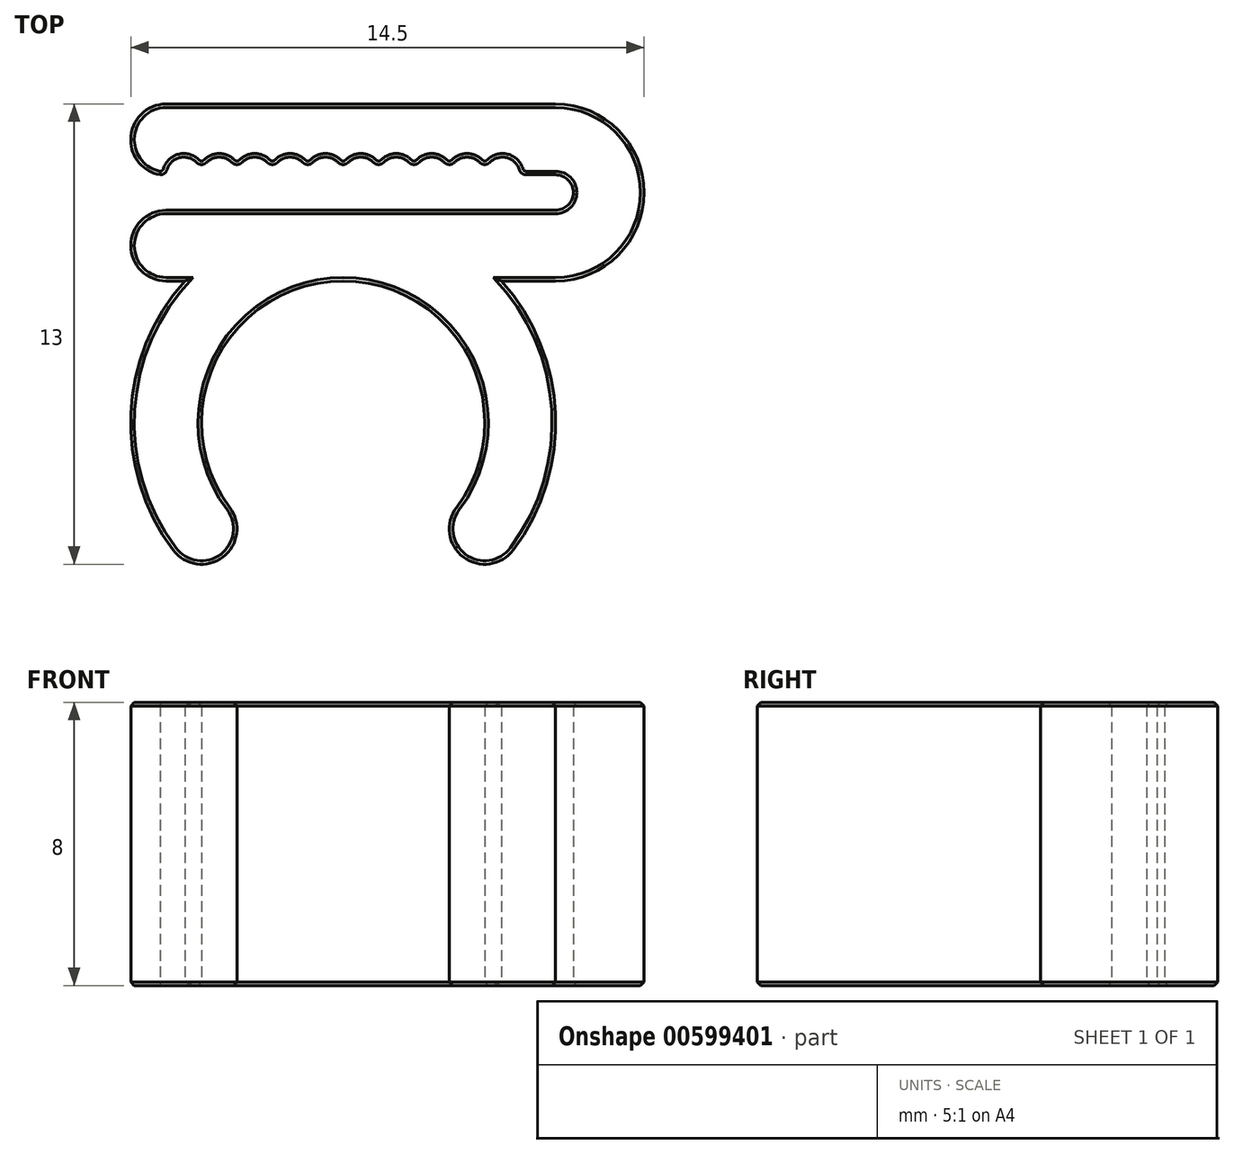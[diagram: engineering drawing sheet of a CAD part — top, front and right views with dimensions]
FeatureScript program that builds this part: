
annotation { "Feature Type Name" : "Feature", "Feature Type Description" : "" }
export const myFeature = defineFeature(function(context is Context, id is Id, definition is map)
    precondition{}
    {
        {
            var Q0;
            Q0=qCreatedBy(makeId("Top.planeOp"),FACE);
            var sketch = newSketch(context, id + "F0", { "sketchPlane" : qUnion([Q0])});
            skCircle(sketch, "E0", {"center": v(0, 0) * mm, "radius": 4 * mm});
            skCircle(sketch, "E1", {"center": v(0, 0) * mm, "radius": 6 * mm});
            skLineSegment(sketch, "E2.bottom", {"start": v(3, -2.65) * mm, "end": v(-3, -2.65) * mm});
            skLineSegment(sketch, "E2.top", {"start": v(3, -6) * mm, "end": v(-3, -6) * mm});
            skLineSegment(sketch, "E2.left", {"start": v(3, -2.65) * mm, "end": v(3, -6) * mm});
            skLineSegment(sketch, "E2.right", {"start": v(-3, -2.65) * mm, "end": v(-3, -6) * mm});
            skPoint(sketch, "E2.middle", {"position": v(0, -4.32) * mm});
            skLineSegment(sketch, "E3.bottom", {"start": v(6, 6) * mm, "end": v(-6, 6) * mm});
            skLineSegment(sketch, "E3.top", {"start": v(6, 4) * mm, "end": v(-6, 4) * mm});
            skLineSegment(sketch, "E3.left", {"start": v(6, 6) * mm, "end": v(6, 4) * mm});
            skLineSegment(sketch, "E3.right", {"start": v(-6, 6) * mm, "end": v(-6, 4) * mm});
            skPoint(sketch, "E3.middle", {"position": v(0, 5) * mm});
            skLineSegment(sketch, "E4.bottom", {"start": v(6, 7) * mm, "end": v(-6, 7) * mm});
            skLineSegment(sketch, "E4.top", {"start": v(6, 9) * mm, "end": v(-6, 9) * mm});
            skLineSegment(sketch, "E4.left", {"start": v(6, 7) * mm, "end": v(6, 9) * mm});
            skLineSegment(sketch, "E4.right", {"start": v(-6, 7) * mm, "end": v(-6, 9) * mm});
            skPoint(sketch, "E4.middle", {"position": v(0, 8) * mm});
            skCircle(sketch, "E5", {"center": v(6, 6.5) * mm, "radius": 2.5 * mm});
            skCircle(sketch, "E6", {"center": v(-4.5, 7) * mm, "radius": 0.5 * mm});
            skCircle(sketch, "E7.1.0.0", {"center": v(-3.5, 7) * mm, "radius": 0.5 * mm});
            skCircle(sketch, "E7.2.0.0", {"center": v(-2.5, 7) * mm, "radius": 0.5 * mm});
            skCircle(sketch, "E7.3.0.0", {"center": v(-1.5, 7) * mm, "radius": 0.5 * mm});
            skCircle(sketch, "E7.4.0.0", {"center": v(-0.5, 7) * mm, "radius": 0.5 * mm});
            skLineSegment(sketch, "E7.direction1", {"start": v(-4.5, 7) * mm, "end": v(-3.5, 7) * mm, "construction": true});
            skCircle(sketch, "E8.0.5.0", {"center": v(0.5, 7) * mm, "radius": 0.5 * mm});
            skCircle(sketch, "E8.0.6.0", {"center": v(1.5, 7) * mm, "radius": 0.5 * mm});
            skCircle(sketch, "E8.0.7.0", {"center": v(2.5, 7) * mm, "radius": 0.5 * mm});
            skCircle(sketch, "E9", {"center": v(6, 6.5) * mm, "radius": 0.5 * mm});
            skCircle(sketch, "E10.0.8.0", {"center": v(3.5, 7) * mm, "radius": 0.5 * mm});
            skCircle(sketch, "E10.0.9.0", {"center": v(4.5, 7) * mm, "radius": 0.5 * mm});
            skSolve(sketch);
        }
        {
            var Q0;
            {var subQ16=sQuery(id+"F0.wireOp",EDGE,"E4.top");Q0=makeQuery(id+"F0.imprint","IMPRINT",FACE,{"disambiguationData":[TD([[makeQuery(id+"F0.imprint","IMPRINT",EDGE,{"derivedFrom":subQ16}),1.0]])]});}
            var Q1;
            {var subQ1=sQuery(id+"F0.wireOp",EDGE,"E4.left");Q1=makeQuery(id+"F0.imprint","IMPRINT",FACE,{"disambiguationData":[TD([[makeQuery(id+"F0.imprint","IMPRINT",EDGE,{"derivedFrom":subQ1}),1.0]])]});}
            var Q2;
            {var subQ0=sQuery(id+"F0.wireOp",EDGE,"E3.left");Q2=makeQuery(id+"F0.imprint","IMPRINT",FACE,{"disambiguationData":[TD([[makeQuery(id+"F0.imprint","IMPRINT",EDGE,{"derivedFrom":subQ0}),1.0]])]});}
            var Q3;
            {var subQ0=sQuery(id+"F0.wireOp",EDGE,"E3.left");Q3=makeQuery(id+"F0.imprint","IMPRINT",FACE,{"disambiguationData":[TD([[makeQuery(id+"F0.imprint","IMPRINT",EDGE,{"derivedFrom":subQ0}),-1.0]])]});}
            var Q4;
            {var subQ0=sQuery(id+"F0.wireOp",EDGE,"E3.bottom");var subQ1=sQuery(id+"F0.wireOp",EDGE,"E1");var subQ2=makeQuery(id+"F0.imprint","INTERSECT",VERTEX,{"derivedFrom":[subQ1,subQ0]});Q4=makeQuery(id+"F0.imprint","IMPRINT",FACE,{"disambiguationData":[TD([[makeQuery(id+"F0.imprint","IMPRINT",EDGE,{"disambiguationData":[TD([[subQ2,1.0]])],"derivedFrom":subQ1}),-1.0]])]});}
            var Q5;
            {var subQ0=sQuery(id+"F0.wireOp",EDGE,"E1");var subQ1=makeQuery(id+"F0.imprint","INTERSECT",VERTEX,{"derivedFrom":[subQ0,sQuery(id+"F0.wireOp",EDGE,"E3.bottom")]});Q5=makeQuery(id+"F0.imprint","IMPRINT",FACE,{"disambiguationData":[TD([[makeQuery(id+"F0.imprint","IMPRINT",EDGE,{"disambiguationData":[TD([[subQ1,1.0]])],"derivedFrom":subQ0}),1.0]])]});}
            var Q6;
            {var subQ5=sQuery(id+"F0.wireOp",EDGE,"E3.right");Q6=makeQuery(id+"F0.imprint","IMPRINT",FACE,{"disambiguationData":[TD([[makeQuery(id+"F0.imprint","IMPRINT",EDGE,{"derivedFrom":subQ5}),1.0]])]});}
            var Q7;
            {var subQ3=sQuery(id+"F0.wireOp",EDGE,"E3.top");var subQ5=sQuery(id+"F0.wireOp",EDGE,"E1");var subQ6=makeQuery(id+"F0.imprint","INTERSECT",VERTEX,{"disambiguationData":[OD(1.0)],"derivedFrom":[subQ5,subQ3]});Q7=makeQuery(id+"F0.imprint","IMPRINT",FACE,{"disambiguationData":[TD([[makeQuery(id+"F0.imprint","IMPRINT",EDGE,{"disambiguationData":[TD([[subQ6,-1.0]])],"derivedFrom":subQ5}),1.0]])]});}
            var Q8;
            {var subQ3=sQuery(id+"F0.wireOp",EDGE,"E3.top");var subQ5=sQuery(id+"F0.wireOp",EDGE,"E1");var subQ7=makeQuery(id+"F0.imprint","INTERSECT",VERTEX,{"disambiguationData":[OD(0.0)],"derivedFrom":[subQ5,subQ3]});Q8=makeQuery(id+"F0.imprint","IMPRINT",FACE,{"disambiguationData":[TD([[makeQuery(id+"F0.imprint","IMPRINT",EDGE,{"disambiguationData":[TD([[subQ7,1.0]])],"derivedFrom":subQ5}),1.0]])]});}
            extrude(context, id + "F1", {"entities" : qUnion([Q0, Q1, Q2, Q3, Q4, Q5, Q6, Q7, Q8]), "depth" : 8 * mm, "offsetDistance" : 25 * mm});
        }
        {
            var Q0;
            Q0=makeQuery(id+"F1.opExtrude","SWEPT_EDGE",EDGE,{"disambiguationData":[OSD([sQuery(id+"F0.wireOp",EDGE,"E4.bottom"),sQuery(id+"F0.wireOp",EDGE,"E6"),sQuery(id+"F0.wireOp",EDGE,"E7.1.0.0")])]});
            var Q1;
            Q1=makeQuery(id+"F1.opExtrude","SWEPT_EDGE",EDGE,{"disambiguationData":[OSD([sQuery(id+"F0.wireOp",EDGE,"E4.bottom"),sQuery(id+"F0.wireOp",EDGE,"E7.1.0.0"),sQuery(id+"F0.wireOp",EDGE,"E7.2.0.0")])]});
            var Q2;
            Q2=makeQuery(id+"F1.opExtrude","SWEPT_EDGE",EDGE,{"disambiguationData":[OSD([sQuery(id+"F0.wireOp",EDGE,"E4.bottom"),sQuery(id+"F0.wireOp",EDGE,"E7.2.0.0"),sQuery(id+"F0.wireOp",EDGE,"E7.3.0.0")])]});
            var Q3;
            Q3=makeQuery(id+"F1.opExtrude","SWEPT_EDGE",EDGE,{"disambiguationData":[OSD([sQuery(id+"F0.wireOp",EDGE,"E4.bottom"),sQuery(id+"F0.wireOp",EDGE,"E7.3.0.0"),sQuery(id+"F0.wireOp",EDGE,"E7.4.0.0")])]});
            var Q4;
            Q4=makeQuery(id+"F1.opExtrude","SWEPT_EDGE",EDGE,{"disambiguationData":[OSD([sQuery(id+"F0.wireOp",EDGE,"E4.bottom"),sQuery(id+"F0.wireOp",EDGE,"E7.4.0.0"),sQuery(id+"F0.wireOp",EDGE,"E8.0.5.0")])]});
            var Q5;
            Q5=makeQuery(id+"F1.opExtrude","SWEPT_EDGE",EDGE,{"disambiguationData":[OSD([sQuery(id+"F0.wireOp",EDGE,"E4.bottom"),sQuery(id+"F0.wireOp",EDGE,"E8.0.5.0"),sQuery(id+"F0.wireOp",EDGE,"E8.0.6.0")])]});
            var Q6;
            Q6=makeQuery(id+"F1.opExtrude","SWEPT_EDGE",EDGE,{"disambiguationData":[OSD([sQuery(id+"F0.wireOp",EDGE,"E4.bottom"),sQuery(id+"F0.wireOp",EDGE,"E8.0.6.0"),sQuery(id+"F0.wireOp",EDGE,"E8.0.7.0")])]});
            var Q7;
            Q7=makeQuery(id+"F1.opExtrude","SWEPT_EDGE",EDGE,{"disambiguationData":[OSD([sQuery(id+"F0.wireOp",EDGE,"E4.bottom"),sQuery(id+"F0.wireOp",EDGE,"E8.0.7.0"),sQuery(id+"F0.wireOp",EDGE,"E10.0.8.0")])]});
            var Q8;
            Q8=makeQuery(id+"F1.opExtrude","SWEPT_EDGE",EDGE,{"disambiguationData":[OSD([sQuery(id+"F0.wireOp",EDGE,"E4.bottom"),sQuery(id+"F0.wireOp",EDGE,"E10.0.8.0"),sQuery(id+"F0.wireOp",EDGE,"E10.0.9.0")])]});
            var Q9;
            Q9=makeQuery(id+"F1.opExtrude","SWEPT_EDGE",EDGE,{"disambiguationData":[OSD([sQuery(id+"F0.wireOp",EDGE,"E4.bottom"),sQuery(id+"F0.wireOp",EDGE,"E6")])]});
            var Q10;
            Q10=makeQuery(id+"F1.opExtrude","SWEPT_EDGE",EDGE,{"disambiguationData":[OSD([sQuery(id+"F0.wireOp",EDGE,"E4.bottom"),sQuery(id+"F0.wireOp",EDGE,"E10.0.9.0")])]});
            fillet(context, id + "F2", {"entities" : qUnion([Q0, Q1, Q2, Q3, Q4, Q5, Q6, Q7, Q8, Q9, Q10]), "radius" : 0.2 * mm, "tangentPropagation" : true, "allowEdgeOverflow" : false});
        }
        {
            var Q0;
            Q0=makeQuery(id+"F1.opExtrude","SWEPT_EDGE",EDGE,{"disambiguationData":[OSD([sQuery(id+"F0.wireOp",EDGE,"E4.bottom"),sQuery(id+"F0.wireOp",EDGE,"E4.right")])]});
            var Q1;
            Q1=makeQuery(id+"F1.opExtrude","SWEPT_EDGE",EDGE,{"disambiguationData":[OSD([sQuery(id+"F0.wireOp",EDGE,"E4.top"),sQuery(id+"F0.wireOp",EDGE,"E4.right")])]});
            var Q2;
            Q2=makeQuery(id+"F1.opExtrude","SWEPT_EDGE",EDGE,{"disambiguationData":[OSD([sQuery(id+"F0.wireOp",EDGE,"E3.bottom"),sQuery(id+"F0.wireOp",EDGE,"E3.right")])]});
            var Q3;
            Q3=makeQuery(id+"F1.opExtrude","SWEPT_EDGE",EDGE,{"disambiguationData":[OSD([sQuery(id+"F0.wireOp",EDGE,"E3.top"),sQuery(id+"F0.wireOp",EDGE,"E3.right")])]});
            var Q4;
            Q4=makeQuery(id+"F1.opExtrude","SWEPT_EDGE",EDGE,{"disambiguationData":[OSD([sQuery(id+"F0.wireOp",EDGE,"E0"),sQuery(id+"F0.wireOp",EDGE,"E2.bottom"),sQuery(id+"F0.wireOp",EDGE,"E2.right")])]});
            var Q5;
            Q5=makeQuery(id+"F1.opExtrude","SWEPT_EDGE",EDGE,{"disambiguationData":[OSD([sQuery(id+"F0.wireOp",EDGE,"E1"),sQuery(id+"F0.wireOp",EDGE,"E2.right")])]});
            var Q6;
            Q6=makeQuery(id+"F1.opExtrude","SWEPT_EDGE",EDGE,{"disambiguationData":[OSD([sQuery(id+"F0.wireOp",EDGE,"E1"),sQuery(id+"F0.wireOp",EDGE,"E2.left")])]});
            var Q7;
            Q7=makeQuery(id+"F1.opExtrude","SWEPT_EDGE",EDGE,{"disambiguationData":[OSD([sQuery(id+"F0.wireOp",EDGE,"E0"),sQuery(id+"F0.wireOp",EDGE,"E2.bottom"),sQuery(id+"F0.wireOp",EDGE,"E2.left")])]});
            fillet(context, id + "F3", {"entities" : qUnion([Q0, Q1, Q2, Q3, Q4, Q5, Q6, Q7]), "radius" : 1 * mm, "tangentPropagation" : true, "allowEdgeOverflow" : false});
        }
        {
            var Q0;
            Q0=makeQuery(id+"F1.opExtrude","CAP_FACE",FACE,{"disambiguationData":[OSD([sQuery(id+"F0.wireOp",EDGE,"E0"),sQuery(id+"F0.wireOp",EDGE,"E1"),sQuery(id+"F0.wireOp",EDGE,"E2.left"),sQuery(id+"F0.wireOp",EDGE,"E2.right"),sQuery(id+"F0.wireOp",EDGE,"E3.bottom"),sQuery(id+"F0.wireOp",EDGE,"E3.top"),sQuery(id+"F0.wireOp",EDGE,"E3.right"),sQuery(id+"F0.wireOp",EDGE,"E4.bottom"),sQuery(id+"F0.wireOp",EDGE,"E4.top"),sQuery(id+"F0.wireOp",EDGE,"E4.right"),sQuery(id+"F0.wireOp",EDGE,"E5"),sQuery(id+"F0.wireOp",EDGE,"E6"),sQuery(id+"F0.wireOp",EDGE,"E7.1.0.0"),sQuery(id+"F0.wireOp",EDGE,"E7.2.0.0"),sQuery(id+"F0.wireOp",EDGE,"E7.3.0.0"),sQuery(id+"F0.wireOp",EDGE,"E7.4.0.0"),sQuery(id+"F0.wireOp",EDGE,"E8.0.5.0"),sQuery(id+"F0.wireOp",EDGE,"E8.0.6.0"),sQuery(id+"F0.wireOp",EDGE,"E8.0.7.0"),sQuery(id+"F0.wireOp",EDGE,"E9"),sQuery(id+"F0.wireOp",EDGE,"E10.0.8.0"),sQuery(id+"F0.wireOp",EDGE,"E10.0.9.0")])],"isStart":false});
            var Q1;
            Q1=makeQuery(id+"F1.opExtrude","CAP_FACE",FACE,{"disambiguationData":[OSD([sQuery(id+"F0.wireOp",EDGE,"E0"),sQuery(id+"F0.wireOp",EDGE,"E1"),sQuery(id+"F0.wireOp",EDGE,"E2.left"),sQuery(id+"F0.wireOp",EDGE,"E2.right"),sQuery(id+"F0.wireOp",EDGE,"E3.bottom"),sQuery(id+"F0.wireOp",EDGE,"E3.top"),sQuery(id+"F0.wireOp",EDGE,"E3.right"),sQuery(id+"F0.wireOp",EDGE,"E4.bottom"),sQuery(id+"F0.wireOp",EDGE,"E4.top"),sQuery(id+"F0.wireOp",EDGE,"E4.right"),sQuery(id+"F0.wireOp",EDGE,"E5"),sQuery(id+"F0.wireOp",EDGE,"E6"),sQuery(id+"F0.wireOp",EDGE,"E7.1.0.0"),sQuery(id+"F0.wireOp",EDGE,"E7.2.0.0"),sQuery(id+"F0.wireOp",EDGE,"E7.3.0.0"),sQuery(id+"F0.wireOp",EDGE,"E7.4.0.0"),sQuery(id+"F0.wireOp",EDGE,"E8.0.5.0"),sQuery(id+"F0.wireOp",EDGE,"E8.0.6.0"),sQuery(id+"F0.wireOp",EDGE,"E8.0.7.0"),sQuery(id+"F0.wireOp",EDGE,"E9"),sQuery(id+"F0.wireOp",EDGE,"E10.0.8.0"),sQuery(id+"F0.wireOp",EDGE,"E10.0.9.0")])],"isStart":true});
            chamfer(context, id + "F4", {"entities" : qUnion([Q0, Q1]), "width" : 0.1 * mm});
        }
    });
